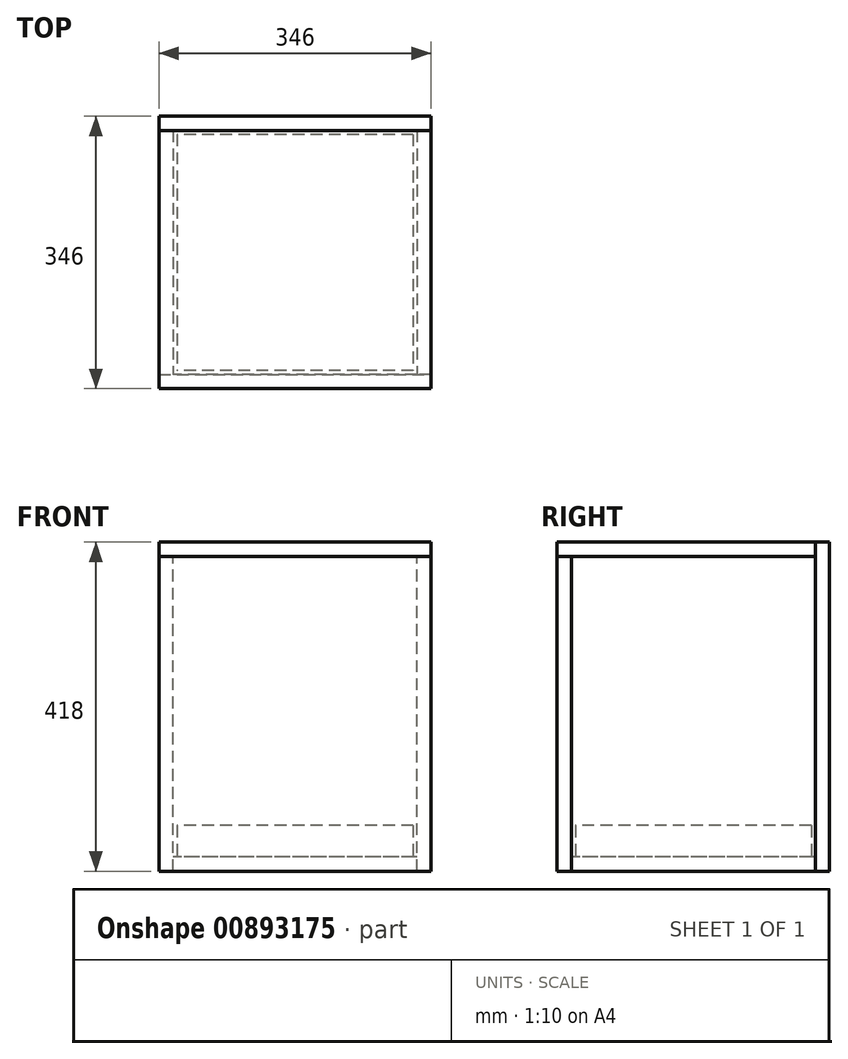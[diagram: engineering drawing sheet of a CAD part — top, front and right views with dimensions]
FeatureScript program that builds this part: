
annotation { "Feature Type Name" : "Feature", "Feature Type Description" : "" }
export const myFeature = defineFeature(function(context is Context, id is Id, definition is map)
    precondition{}
    {
        {
            var Q0;
            Q0=qCreatedBy(makeId("Top.planeOp"),FACE);
            var sketch = newSketch(context, id + "F0", { "sketchPlane" : qUnion([Q0])});
            skLineSegment(sketch, "E0.bottom", {"start": v(150, 150) * mm, "end": v(-150, 150) * mm});
            skLineSegment(sketch, "E0.top", {"start": v(150, -150) * mm, "end": v(-150, -150) * mm});
            skLineSegment(sketch, "E0.left", {"start": v(150, 150) * mm, "end": v(150, -150) * mm});
            skLineSegment(sketch, "E0.right", {"start": v(-150, 150) * mm, "end": v(-150, -150) * mm});
            skPoint(sketch, "E0.middle", {"position": v(0, 0) * mm});
            skLineSegment(sketch, "E1.bottom", {"start": v(155, 155) * mm, "end": v(-155, 155) * mm});
            skLineSegment(sketch, "E1.top", {"start": v(155, -155) * mm, "end": v(-155, -155) * mm});
            skLineSegment(sketch, "E1.left", {"start": v(155, 155) * mm, "end": v(155, -155) * mm});
            skLineSegment(sketch, "E1.right", {"start": v(-155, 155) * mm, "end": v(-155, -155) * mm});
            skSolve(sketch);
        }
        {
            var Q0;
            Q0=makeQuery(id+"F0.imprint","IMPRINT",FACE,{"disambiguationData":[TD([[makeQuery(id+"F0.imprint","IMPRINT",EDGE,{"derivedFrom":sQuery(id+"F0.wireOp",EDGE,"E0.bottom")}),1.0]])]});
            extrude(context, id + "F1", {"entities" : qUnion([Q0]), "depth" : 40 * mm, "offsetDistance" : 25 * mm});
        }
        {
            var Q0;
            Q0=makeQuery(id+"F0.imprint","IMPRINT",FACE,{"disambiguationData":[TD([[makeQuery(id+"F0.imprint","IMPRINT",EDGE,{"derivedFrom":sQuery(id+"F0.wireOp",EDGE,"E0.bottom")}),-1.0]])]});
            var Q1;
            Q1=makeQuery(id+"F0.imprint","IMPRINT",FACE,{"disambiguationData":[TD([[makeQuery(id+"F0.imprint","IMPRINT",EDGE,{"derivedFrom":sQuery(id+"F0.wireOp",EDGE,"E0.bottom")}),1.0]])]});
            extrude(context, id + "F2", {"entities" : qUnion([Q0, Q1]), "oppositeDirection" : true, "depth" : 18 * mm, "offsetDistance" : 25 * mm});
        }
        {
            var Q0;
            Q0=makeQuery(id+"F2.opExtrude","SWEPT_FACE",FACE,{"disambiguationData":[OSD([sQuery(id+"F0.wireOp",EDGE,"E1.right")])]});
            var sketch = newSketch(context, id + "F3", { "sketchPlane" : qUnion([Q0])});
            skLineSegment(sketch, "E2.bottom", {"start": v(-155, -18) * mm, "end": v(155, -18) * mm});
            skLineSegment(sketch, "E2.top", {"start": v(-155, 382) * mm, "end": v(155, 382) * mm});
            skLineSegment(sketch, "E2.left", {"start": v(-155, -18) * mm, "end": v(-155, 382) * mm});
            skLineSegment(sketch, "E2.right", {"start": v(155, -18) * mm, "end": v(155, 382) * mm});
            skSolve(sketch);
        }
        {
            var Q0;
            {var subQ0=sQuery(id+"F3.wireOp",EDGE,"E2.bottom");Q0=makeQuery(id+"F3.imprint","IMPRINT",FACE,{"disambiguationData":[TD([[makeQuery(id+"F3.imprint","IMPRINT",EDGE,{"derivedFrom":subQ0}),1.0]])]});}
            var Q1;
            {var subQ0=sQuery(id+"F3.wireOp",EDGE,"E2.top");Q1=makeQuery(id+"F3.imprint","IMPRINT",FACE,{"disambiguationData":[TD([[makeQuery(id+"F3.imprint","IMPRINT",EDGE,{"derivedFrom":subQ0}),-1.0]])]});}
            extrude(context, id + "F4", {"entities" : qUnion([Q0, Q1]), "depth" : 18 * mm, "offsetDistance" : 25 * mm});
        }
        {
            var Q0;
            Q0=makeQuery(id+"F4.opExtrude","SWEPT_BODY",BODY,{"disambiguationData":[OSD([sQuery(id+"F3.wireOp",EDGE,"E2.bottom"),sQuery(id+"F3.wireOp",EDGE,"E2.top"),sQuery(id+"F3.wireOp",EDGE,"E2.left"),sQuery(id+"F3.wireOp",EDGE,"E2.right")])]});
            var Q1;
            Q1=qCreatedBy(makeId("Right.planeOp"),FACE);
            mirror(context, id + "F5", {"entities" : qUnion([Q0]), "mirrorPlane" : qUnion([Q1])});
        }
        {
            var Q0;
            Q0=makeQuery(id+"F2.opExtrude","SWEPT_FACE",FACE,{"disambiguationData":[OSD([sQuery(id+"F0.wireOp",EDGE,"E1.top")])]});
            var sketch = newSketch(context, id + "F6", { "sketchPlane" : qUnion([Q0])});
            skLineSegment(sketch, "E3.bottom", {"start": v(-173, -18) * mm, "end": v(173, -18) * mm});
            skLineSegment(sketch, "E3.top", {"start": v(-173, 382) * mm, "end": v(173, 382) * mm});
            skLineSegment(sketch, "E3.left", {"start": v(-173, -18) * mm, "end": v(-173, 382) * mm});
            skLineSegment(sketch, "E3.right", {"start": v(173, -18) * mm, "end": v(173, 382) * mm});
            skSolve(sketch);
        }
        {
            var Q0;
            Q0=makeQuery(id+"F6.imprint","IMPRINT",FACE,{"disambiguationData":[TD([[makeQuery(id+"F6.imprint","IMPRINT",EDGE,{"derivedFrom":sQuery(id+"F6.wireOp",EDGE,"E3.top")}),-1.0]])]});
            var Q1;
            {var subQ1=sQuery(id+"F0.wireOp",EDGE,"E1.top");Q1=makeQuery(id+"F6.imprint","IMPRINT",FACE,{"disambiguationData":[TD([[makeQuery(id+"F6.imprint","IMPRINT",EDGE,{"derivedFrom":makeQuery(id+"F2.opExtrude","CAP_EDGE",EDGE,{"disambiguationData":[OSD([subQ1])],"isStart":true})}),1.0]])]});}
            extrude(context, id + "F7", {"entities" : qUnion([Q0, Q1]), "depth" : 18 * mm, "offsetDistance" : 25 * mm});
        }
        {
            var Q0;
            Q0=makeQuery(id+"F7.opExtrude","SWEPT_FACE",FACE,{"disambiguationData":[OSD([sQuery(id+"F6.wireOp",EDGE,"E3.top")])]});
            var sketch = newSketch(context, id + "F8", { "sketchPlane" : qUnion([Q0])});
            skLineSegment(sketch, "E4.bottom", {"start": v(173, -173) * mm, "end": v(-173, -173) * mm});
            skLineSegment(sketch, "E4.top", {"start": v(173, 155) * mm, "end": v(-173, 155) * mm});
            skLineSegment(sketch, "E4.left", {"start": v(173, -173) * mm, "end": v(173, 155) * mm});
            skLineSegment(sketch, "E4.right", {"start": v(-173, -173) * mm, "end": v(-173, 155) * mm});
            skSolve(sketch);
        }
        {
            var Q0;
            {var subQ0=sQuery(id+"F8.wireOp",EDGE,"E4.bottom");Q0=makeQuery(id+"F8.imprint","IMPRINT",FACE,{"disambiguationData":[TD([[makeQuery(id+"F8.imprint","IMPRINT",EDGE,{"derivedFrom":subQ0}),1.0]])]});}
            var Q1;
            {var subQ0=sQuery(id+"F8.wireOp",EDGE,"E4.top");Q1=makeQuery(id+"F8.imprint","IMPRINT",FACE,{"disambiguationData":[TD([[makeQuery(id+"F8.imprint","IMPRINT",EDGE,{"derivedFrom":subQ0}),1.0]])]});}
            extrude(context, id + "F9", {"entities" : qUnion([Q0, Q1]), "depth" : 18 * mm, "offsetDistance" : 25 * mm});
        }
        {
            var Q0;
            Q0=makeQuery(id+"F5.opPattern","COPY",FACE,{"derivedFrom":makeQuery(id+"F4.opExtrude","SWEPT_FACE",FACE,{"disambiguationData":[OSD([sQuery(id+"F3.wireOp",EDGE,"E2.left")])]}),"instanceName":"1"});
            var sketch = newSketch(context, id + "F10", { "sketchPlane" : qUnion([Q0])});
            skLineSegment(sketch, "E5.bottom", {"start": v(173, -18) * mm, "end": v(-173, -18) * mm});
            skLineSegment(sketch, "E5.top", {"start": v(173, 400) * mm, "end": v(-173, 400) * mm});
            skLineSegment(sketch, "E5.left", {"start": v(173, -18) * mm, "end": v(173, 400) * mm});
            skLineSegment(sketch, "E5.right", {"start": v(-173, -18) * mm, "end": v(-173, 400) * mm});
            skSolve(sketch);
        }
        {
            var Q0;
            {var subQ1=sQuery(id+"F3.wireOp",EDGE,"E2.left");var subQ2=makeQuery(id+"F5.opPattern","COPY",EDGE,{"derivedFrom":makeQuery(id+"F4.opExtrude","CAP_EDGE",EDGE,{"disambiguationData":[OSD([subQ1])],"isStart":true}),"instanceName":"1"});Q0=makeQuery(id+"F10.imprint","IMPRINT",FACE,{"disambiguationData":[TD([[makeQuery(id+"F10.imprint","IMPRINT",EDGE,{"derivedFrom":subQ2}),1.0]])]});}
            var Q1;
            {var subQ1=sQuery(id+"F10.wireOp",EDGE,"E5.top");Q1=makeQuery(id+"F10.imprint","IMPRINT",FACE,{"disambiguationData":[TD([[makeQuery(id+"F10.imprint","IMPRINT",EDGE,{"derivedFrom":subQ1}),1.0]])]});}
            extrude(context, id + "F11", {"entities" : qUnion([Q0, Q1]), "depth" : 18 * mm, "offsetDistance" : 25 * mm});
        }
    });
